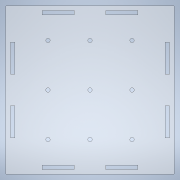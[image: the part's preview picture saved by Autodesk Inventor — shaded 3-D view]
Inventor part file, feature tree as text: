
AUTODESK INVENTOR PART (.ipt)
format: ipt  version: 2020 (Build 240168000, 168)  size: 194,560 bytes
history: native  units: mm
features: sketch x11, hole x9, extrude x2
ambient origin geometry x8: Origin, YZ Plane, XZ Plane, XY Plane, X Axis, Y Axis, Z Axis, Center Point
bodies: Solid1 (feature_tree)
feature tree (22):
  extrude  "Extrusion1"  Depth=106.0mm
  hole  "Hole1"  [1 undecoded]
  sketch  "Sketch3"  dims[d7=1.0mm d8=1.0mm]
  hole  "Hole2"  [1 undecoded]
  hole  "Hole3"  [1 undecoded]
  hole  "Hole4"  [1 undecoded]
  hole  "Hole5"  [1 undecoded]
  hole  "Hole6"  [1 undecoded]
  hole  "Hole7"  [1 undecoded]
  hole  "Hole8"  [1 undecoded]
  hole  "Hole9"  [1 undecoded]
  extrude  "Extrusion2"  Depth=3.0mm
  sketch  "Sketch1"  dims[d0=106.0mm d1=106.0mm]
  sketch  "Sketch2"  dims[d4=3.0mm d5=0.0mm d6=1.0mm]
  sketch  "Sketch5"  dims[d9=1.0mm d10=1.0mm]
  sketch  "Sketch6"  dims[d11=1.0mm d12=1.0mm]
  sketch  "Sketch7"  dims[d13=1.0mm d14=1.0mm]
  sketch  "Sketch8"  dims[d15=3.0mm d16=6.0mm d17=4.0mm d18=2.0mm d19=90.0deg d20=8.0mm d21=20.594885mm d22=3.0mm]
  sketch  "Sketch9"  dims[d23=3.0mm d24=3.0mm]
  sketch  "Sketch10"  dims[d25=3.0mm d26=3.0mm]
  sketch  "Sketch11"  dims[d27=3.0mm d28=3.0mm]
  sketch  "Sketch12"  dims[d29=3.0mm d30=3.0mm d31=6.0mm d32=4.0mm d33=2.0mm d34=90.0deg d35=8.0mm d36=20.594885mm d37=3.0mm d38=3.0mm d39=6.0mm d40=4.0mm d41=2.0mm d42=90.0deg d43=8.0mm d44=20.594885mm d45=3.0mm d46=3.0mm d47=6.0mm d48=4.0mm d49=2.0mm d50=90.0deg d51=8.0mm d52=20.594885mm d53=3.0mm d54=3.0mm d55=6.0mm d56=4.0mm d57=2.0mm d58=90.0deg d59=8.0mm d60=20.594885mm d61=3.0mm d62=3.0mm d63=6.0mm d64=4.0mm d65=2.0mm d66=90.0deg d67=8.0mm d68=20.594885mm d69=3.0mm d70=3.0mm d71=6.0mm d72=4.0mm d73=2.0mm d74=90.0deg d75=8.0mm d76=20.594885mm d77=3.0mm d78=3.0mm d79=6.0mm d80=4.0mm d81=2.0mm d82=90.0deg d83=8.0mm d84=20.594885mm d85=3.0mm d86=3.0mm d87=6.0mm d88=4.0mm d89=2.0mm d90=90.0deg d91=8.0mm d92=20.594885mm d99=112.0mm d100=112.0mm d101=3.0mm d102=0.0mm d103=0.5mm d104=0.872665mm]
note: 9 required parameter values undecoded (feature->parameter linkage not recoverable at this tier; creation-order binding heuristic only, values carry confidence <= 0.55)
